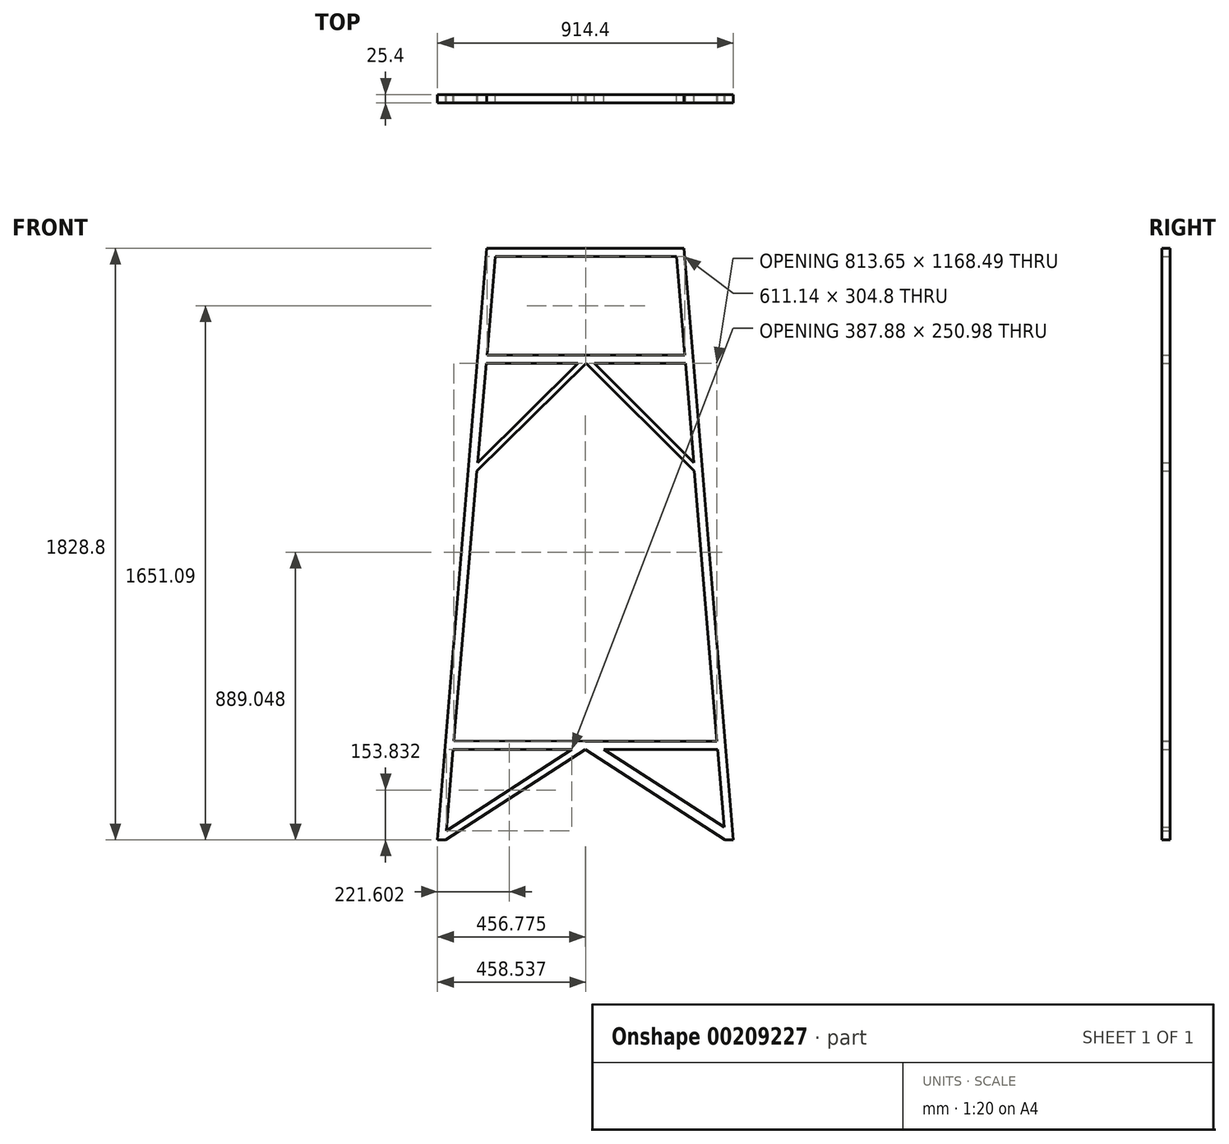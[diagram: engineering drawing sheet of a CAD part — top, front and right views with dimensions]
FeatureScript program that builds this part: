
annotation { "Feature Type Name" : "Feature", "Feature Type Description" : "" }
export const myFeature = defineFeature(function(context is Context, id is Id, definition is map)
    precondition{}
    {
        {
            var Q0;
            Q0=qCreatedBy(makeId("Front.planeOp"),FACE);
            var sketch = newSketch(context, id + "F0", { "sketchPlane" : qUnion([Q0])});
            skLineSegment(sketch, "E0", {"start": v(-304.8, 358.27) * mm, "end": v(0, 358.27) * mm});
            skLineSegment(sketch, "E1", {"start": v(0, 358.27) * mm, "end": v(304.8, 358.27) * mm});
            skLineSegment(sketch, "E2", {"start": v(304.8, 358.27) * mm, "end": v(457.2, -1470.53) * mm});
            skLineSegment(sketch, "E3", {"start": v(-457.2, -1470.53) * mm, "end": v(-304.8, 358.27) * mm});
            skLineSegment(sketch, "E4", {"start": v(281.5, 332.96) * mm, "end": v(306.9, 28.16) * mm});
            skPoint(sketch, "E5", {"position": v(0, -1165.73) * mm});
            skLineSegment(sketch, "E6", {"start": v(-409.52, -1191.2) * mm, "end": v(-41.66, -1191.2) * mm});
            skPoint(sketch, "E7", {"position": v(0, -1191.13) * mm});
            skLineSegment(sketch, "E8", {"start": v(-431.8, -1470.53) * mm, "end": v(0, -1191.13) * mm});
            skLineSegment(sketch, "E9", {"start": v(431.8, -1470.53) * mm, "end": v(0, -1191.13) * mm});
            skLineSegment(sketch, "E10", {"start": v(-457.2, -1470.53) * mm, "end": v(-431.8, -1470.53) * mm});
            skLineSegment(sketch, "E11", {"start": v(431.8, -1470.53) * mm, "end": v(457.2, -1470.53) * mm});
            skLineSegment(sketch, "E12.trimOffspring", {"start": v(-407.25, -1164.94) * mm, "end": v(-335.18, -330.2) * mm});
            skLineSegment(sketch, "E13", {"start": v(0, -1165.73) * mm, "end": v(406.4, -1165.73) * mm});
            skLineSegment(sketch, "E14", {"start": v(0, -1165.73) * mm, "end": v(-407.28, -1164.94) * mm});
            skPoint(sketch, "E15", {"position": v(-407.28, -1164.94) * mm});
            skLineSegment(sketch, "E16", {"start": v(-409.52, -1191.2) * mm, "end": v(-429.54, -1442.19) * mm});
            skLineSegment(sketch, "E17.trimOffspring", {"start": v(408.52, -1191.2) * mm, "end": v(428.54, -1431.36) * mm});
            skLineSegment(sketch, "E18", {"start": v(-41.66, -1191.2) * mm, "end": v(-429.54, -1442.19) * mm});
            skLineSegment(sketch, "E19.trimOffspring", {"start": v(-0.12, -1191.2) * mm, "end": v(0.12, -1191.2) * mm});
            skLineSegment(sketch, "E20", {"start": v(57.4, -1191.2) * mm, "end": v(428.54, -1431.36) * mm});
            skLineSegment(sketch, "E21.trimOffspring", {"start": v(57.4, -1191.2) * mm, "end": v(408.52, -1191.2) * mm});
            skLineSegment(sketch, "E22", {"start": v(-277.92, 332.88) * mm, "end": v(281.5, 332.96) * mm});
            skLineSegment(sketch, "E23", {"start": v(-304.23, 28.16) * mm, "end": v(306.9, 28.16) * mm});
            skPoint(sketch, "E24", {"position": v(0, 0) * mm});
            skLineSegment(sketch, "E25", {"start": v(1.7, 2.76) * mm, "end": v(0, 2.76) * mm});
            skLineSegment(sketch, "E26", {"start": v(27.1, 2.73) * mm, "end": v(309.06, 2.38) * mm});
            skLineSegment(sketch, "E27.trimOffspring", {"start": v(309.06, 2.38) * mm, "end": v(334.66, -304.8) * mm});
            skLineSegment(sketch, "E28.trimOffspring", {"start": v(-304.23, 28.16) * mm, "end": v(-277.92, 332.88) * mm});
            skLineSegment(sketch, "E29", {"start": v(0, 358.27) * mm, "end": v(0, -1165.73) * mm, "construction": true});
            skPoint(sketch, "E30", {"position": v(0, -304.8) * mm});
            skPoint(sketch, "E31", {"position": v(-332.98, -304.8) * mm});
            skPoint(sketch, "E32", {"position": v(334.66, -304.8) * mm});
            skPoint(sketch, "E33", {"position": v(0, -330.2) * mm});
            skPoint(sketch, "E34", {"position": v(336.77, -330.2) * mm});
            skPoint(sketch, "E35", {"position": v(-335.18, -330.2) * mm});
            skLineSegment(sketch, "E36", {"start": v(-335.18, -330.2) * mm, "end": v(1.7, 2.76) * mm});
            skLineSegment(sketch, "E37", {"start": v(336.77, -330.2) * mm, "end": v(1.7, 2.76) * mm});
            skPoint(sketch, "E38", {"position": v(-23.7, 2.76) * mm});
            skPoint(sketch, "E39", {"position": v(27.1, 2.73) * mm});
            skLineSegment(sketch, "E40", {"start": v(-332.98, -304.8) * mm, "end": v(-23.7, 2.76) * mm});
            skLineSegment(sketch, "E41", {"start": v(334.66, -304.8) * mm, "end": v(27.1, 2.73) * mm});
            skLineSegment(sketch, "E42.trimOffspring", {"start": v(-23.7, 2.76) * mm, "end": v(-306.43, 2.76) * mm});
            skLineSegment(sketch, "E43.trimOffspring", {"start": v(-332.98, -304.8) * mm, "end": v(-306.43, 2.76) * mm});
            skLineSegment(sketch, "E44.trimOffspring", {"start": v(336.77, -330.2) * mm, "end": v(406.4, -1165.73) * mm});
            skPoint(sketch, "E45", {"position": v(-332.3, 28.16) * mm});
            skPoint(sketch, "E46", {"position": v(309.06, 2.38) * mm});
            skPoint(sketch, "E47", {"position": v(332.3, 28.16) * mm});
            skSolve(sketch);
        }
        {
            var Q0;
            {var subQ0=sQuery(id+"F0.wireOp",EDGE,"E2");var subQ1=sQuery(id+"F0.wireOp",EDGE,"E1");var subQ2=makeQuery(id+"F0.imprint","INTERSECT",VERTEX,{"derivedFrom":[subQ1,subQ0]});Q0=makeQuery(id+"F0.imprint","IMPRINT",FACE,{"disambiguationData":[TD([[makeQuery(id+"F0.imprint","IMPRINT",EDGE,{"disambiguationData":[TD([[subQ2,1.0]])],"derivedFrom":subQ1}),-1.0]])]});}
            var Q1;
            {var subQ0=sQuery(id+"F0.wireOp",EDGE,"CxdlK8mQ-9sQV-PWuO-nWA8-7TpWkvv8Couq");var subQ1=sQuery(id+"F0.wireOp",EDGE,"E2");var subQ2=makeQuery(id+"F0.imprint","INTERSECT",VERTEX,{"derivedFrom":[subQ1,subQ0]});Q1=makeQuery(id+"F0.imprint","IMPRINT",FACE,{"disambiguationData":[TD([[makeQuery(id+"F0.imprint","IMPRINT",EDGE,{"disambiguationData":[TD([[subQ2,1.0]])],"derivedFrom":subQ1}),-1.0]])]});}
            var Q2;
            {var subQ0=sQuery(id+"F0.wireOp",EDGE,"E3");var subQ1=sQuery(id+"F0.wireOp",EDGE,"CxdlK8mQ-9sQV-PWuO-nWA8-7TpWkvv8Couq");var subQ2=makeQuery(id+"F0.imprint","INTERSECT",VERTEX,{"derivedFrom":[subQ1,subQ0]});Q2=makeQuery(id+"F0.imprint","IMPRINT",FACE,{"disambiguationData":[TD([[makeQuery(id+"F0.imprint","IMPRINT",EDGE,{"disambiguationData":[TD([[subQ2,1.0]])],"derivedFrom":subQ1}),-1.0]])]});}
            var Q3;
            {var subQ0=sQuery(id+"F0.wireOp",EDGE,"ZHtUtwkl-PTfP-ZYUE-q12q-orDdZN2A8tmq");var subQ1=sQuery(id+"F0.wireOp",EDGE,"E2");var subQ2=makeQuery(id+"F0.imprint","INTERSECT",VERTEX,{"derivedFrom":[subQ1,subQ0]});Q3=makeQuery(id+"F0.imprint","IMPRINT",FACE,{"disambiguationData":[TD([[makeQuery(id+"F0.imprint","IMPRINT",EDGE,{"disambiguationData":[TD([[subQ2,-1.0]])],"derivedFrom":subQ1}),-1.0]])]});}
            var Q4;
            {var subQ0=sQuery(id+"F0.wireOp",EDGE,"E4");var subQ1=sQuery(id+"F0.wireOp",EDGE,"CxdlK8mQ-9sQV-PWuO-nWA8-7TpWkvv8Couq");var subQ2=makeQuery(id+"F0.imprint","INTERSECT",VERTEX,{"derivedFrom":[subQ1,subQ0]});Q4=makeQuery(id+"F0.imprint","IMPRINT",FACE,{"disambiguationData":[TD([[makeQuery(id+"F0.imprint","IMPRINT",EDGE,{"disambiguationData":[TD([[subQ2,-1.0]])],"derivedFrom":subQ1}),-1.0]])]});}
            extrude(context, id + "F1", {"entities" : qUnion([Q0, Q1, Q2, Q3, Q4]), "depth" : 25.4 * mm});
        }
    });
